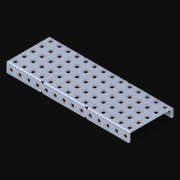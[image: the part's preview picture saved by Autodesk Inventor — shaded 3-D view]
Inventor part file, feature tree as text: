
AUTODESK INVENTOR PART (.ipt)
format: ipt  version: 2021 (Build 250183000, 183)  size: 1,781,760 bytes
history: native  units: in
note: dims shown in document units (in); Inventor stores cm internally (conversion verified against a paired STEP export)
features: extrude x99, other x99, sketch x4, pattern_linear x3
ambient origin geometry x8: Origin, YZ Plane, XZ Plane, XY Plane, X Axis, Y Axis, Z Axis, Center Point
bodies: Solid1 (feature_tree)
feature tree (205):
  pattern_linear  "Rectangular Pattern1"  Spacing1=0.182in  [1 undecoded]
  pattern_linear  "Rectangular Pattern2"  Spacing1=0.046in  [1 undecoded]
  pattern_linear  "Rectangular Pattern3"  Spacing1=0.5in  [1 undecoded]
  extrude  "Extrusion1"  Depth=0.046in
  sketch  "Sketch1"  dims[d0=0.182in]
  other  "Srf1"
  sketch  "Sketch2"  dims[d1=0.046in d2=0.0in]
  other  "Srf2"
  sketch  "Sketch3"  dims[d3=0.182in]
  other  "Srf3"
  other  "Srf4"
  other  "Srf5"
  other  "Srf6"
  other  "Srf7"
  other  "Srf8"
  other  "Srf9"
  other  "Srf10"
  other  "Srf11"
  other  "Srf12"
  other  "Srf13"
  other  "Srf14"
  other  "Srf15"
  other  "Srf16"
  other  "Srf38"
  other  "Srf39"
  other  "Srf40"
  other  "Srf41"
  other  "Srf42"
  other  "Srf43"
  other  "Srf44"
  other  "Srf45"
  other  "Srf46"
  other  "Srf47"
  other  "Srf48"
  other  "Srf49"
  other  "Srf50"
  other  "Srf72"
  other  "Srf73"
  other  "Srf74"
  other  "Srf75"
  other  "Srf76"
  other  "Srf77"
  other  "Srf78"
  other  "Srf79"
  other  "Srf80"
  other  "Srf81"
  other  "Srf82"
  other  "Srf83"
  other  "Srf84"
  other  "Srf85"
  other  "Srf107"
  other  "Srf108"
  other  "Srf109"
  other  "Srf110"
  other  "Srf111"
  other  "Srf112"
  other  "Srf113"
  other  "Srf114"
  other  "Srf115"
  other  "Srf116"
  other  "Srf117"
  other  "Srf118"
  other  "Srf119"
  other  "Srf120"
  other  "Srf142"
  other  "Srf143"
  other  "Srf144"
  other  "Srf145"
  other  "Srf146"
  other  "Srf147"
  other  "Srf148"
  other  "Srf149"
  other  "Srf150"
  other  "Srf151"
  other  "Srf152"
  other  "Srf153"
  other  "Srf154"
  other  "Srf155"
  other  "Srf177"
  other  "Srf178"
  other  "Srf179"
  other  "Srf180"
  other  "Srf181"
  other  "Srf182"
  other  "Srf183"
  other  "Srf184"
  other  "Srf185"
  other  "Srf186"
  other  "Srf187"
  other  "Srf188"
  other  "Srf189"
  other  "Srf190"
  other  "Srf212"
  other  "Srf213"
  other  "Srf214"
  other  "Srf215"
  other  "Srf216"
  other  "Srf217"
  other  "Srf218"
  other  "Srf219"
  other  "Srf220"
  other  "Srf221"
  other  "Srf222"
  other  "Srf223"
  other  "Srf224"
  sketch  "Sketch4"  dims[d4=0.046in d5=0.0in d6=0.182in d7=0.046in d8=0.0in d11=0.5in d12=5.5118in d14=0.5in d15=1.9685in d17=0.5in d18=5.5118in d20=0.5in d21=10.5in d22=0.0in]
  parser-record x1  (decoder bookkeeping rows leaked as tree rows — omitted from the tree; the rows remain in map.json)
  extrude  "ExtrusionSrf1"  Depth=0.046in
  extrude  "ExtrusionSrf2"  Depth=0.046in
  extrude  "ExtrusionSrf3"  Depth=0.046in
  extrude  "ExtrusionSrf4"  Depth=0.046in
  extrude  "ExtrusionSrf5"  Depth=0.046in
  extrude  "ExtrusionSrf6"  TaperAngle=0.0deg  [1 undecoded]
  extrude  "ExtrusionSrf7"  [1 undecoded]
  extrude  "ExtrusionSrf8"  [1 undecoded]
  extrude  "ExtrusionSrf9"  [1 undecoded]
  extrude  "ExtrusionSrf10"  [1 undecoded]
  extrude  "ExtrusionSrf11"  [1 undecoded]
  extrude  "ExtrusionSrf12"  [1 undecoded]
  extrude  "ExtrusionSrf13"  [1 undecoded]
  extrude  "ExtrusionSrf14"  [1 undecoded]
  extrude  "ExtrusionSrf15"  [1 undecoded]
  extrude  "ExtrusionSrf16"  [1 undecoded]
  extrude  "ExtrusionSrf38"  [1 undecoded]
  extrude  "ExtrusionSrf39"  [1 undecoded]
  extrude  "ExtrusionSrf40"  [1 undecoded]
  extrude  "ExtrusionSrf41"  [1 undecoded]
  extrude  "ExtrusionSrf42"  [1 undecoded]
  extrude  "ExtrusionSrf43"  [1 undecoded]
  extrude  "ExtrusionSrf44"  [1 undecoded]
  extrude  "ExtrusionSrf45"  [1 undecoded]
  extrude  "ExtrusionSrf46"  [1 undecoded]
  extrude  "ExtrusionSrf47"  [1 undecoded]
  extrude  "ExtrusionSrf48"  [1 undecoded]
  extrude  "ExtrusionSrf49"  [1 undecoded]
  extrude  "ExtrusionSrf50"  [1 undecoded]
  extrude  "ExtrusionSrf72"  [1 undecoded]
  extrude  "ExtrusionSrf73"  [1 undecoded]
  extrude  "ExtrusionSrf74"  [1 undecoded]
  extrude  "ExtrusionSrf75"  [1 undecoded]
  extrude  "ExtrusionSrf76"  [1 undecoded]
  extrude  "ExtrusionSrf77"  [1 undecoded]
  extrude  "ExtrusionSrf78"  [1 undecoded]
  extrude  "ExtrusionSrf79"  [1 undecoded]
  extrude  "ExtrusionSrf80"  [1 undecoded]
  extrude  "ExtrusionSrf81"  [1 undecoded]
  extrude  "ExtrusionSrf82"  [1 undecoded]
  extrude  "ExtrusionSrf83"  [1 undecoded]
  extrude  "ExtrusionSrf84"  [1 undecoded]
  extrude  "ExtrusionSrf85"  [1 undecoded]
  extrude  "ExtrusionSrf107"  [1 undecoded]
  extrude  "ExtrusionSrf108"  [1 undecoded]
  extrude  "ExtrusionSrf109"  [1 undecoded]
  extrude  "ExtrusionSrf110"  [1 undecoded]
  extrude  "ExtrusionSrf111"  [1 undecoded]
  extrude  "ExtrusionSrf112"  [1 undecoded]
  extrude  "ExtrusionSrf113"  [1 undecoded]
  extrude  "ExtrusionSrf114"  [1 undecoded]
  extrude  "ExtrusionSrf115"  [1 undecoded]
  extrude  "ExtrusionSrf116"  [1 undecoded]
  extrude  "ExtrusionSrf117"  [1 undecoded]
  extrude  "ExtrusionSrf118"  [1 undecoded]
  extrude  "ExtrusionSrf119"  [1 undecoded]
  extrude  "ExtrusionSrf120"  [1 undecoded]
  extrude  "ExtrusionSrf142"  [1 undecoded]
  extrude  "ExtrusionSrf143"  [1 undecoded]
  extrude  "ExtrusionSrf144"  [1 undecoded]
  extrude  "ExtrusionSrf145"  [1 undecoded]
  extrude  "ExtrusionSrf146"  [1 undecoded]
  extrude  "ExtrusionSrf147"  [1 undecoded]
  extrude  "ExtrusionSrf148"  [1 undecoded]
  extrude  "ExtrusionSrf149"  [1 undecoded]
  extrude  "ExtrusionSrf150"  [1 undecoded]
  extrude  "ExtrusionSrf151"  [1 undecoded]
  extrude  "ExtrusionSrf152"  [1 undecoded]
  extrude  "ExtrusionSrf153"  [1 undecoded]
  extrude  "ExtrusionSrf154"  [1 undecoded]
  extrude  "ExtrusionSrf155"  [1 undecoded]
  extrude  "ExtrusionSrf177"  [1 undecoded]
  extrude  "ExtrusionSrf178"  [1 undecoded]
  extrude  "ExtrusionSrf179"  [1 undecoded]
  extrude  "ExtrusionSrf180"  [1 undecoded]
  extrude  "ExtrusionSrf181"  [1 undecoded]
  extrude  "ExtrusionSrf182"  [1 undecoded]
  extrude  "ExtrusionSrf183"  [1 undecoded]
  extrude  "ExtrusionSrf184"  [1 undecoded]
  extrude  "ExtrusionSrf185"  [1 undecoded]
  extrude  "ExtrusionSrf186"  [1 undecoded]
  extrude  "ExtrusionSrf187"  [1 undecoded]
  extrude  "ExtrusionSrf188"  [1 undecoded]
  extrude  "ExtrusionSrf189"  [1 undecoded]
  extrude  "ExtrusionSrf190"  [1 undecoded]
  extrude  "ExtrusionSrf212"  [1 undecoded]
  extrude  "ExtrusionSrf213"  [1 undecoded]
  extrude  "ExtrusionSrf214"  [1 undecoded]
  extrude  "ExtrusionSrf215"  [1 undecoded]
  extrude  "ExtrusionSrf216"  [1 undecoded]
  extrude  "ExtrusionSrf217"  [1 undecoded]
  extrude  "ExtrusionSrf218"  [1 undecoded]
  extrude  "ExtrusionSrf219"  [1 undecoded]
  extrude  "ExtrusionSrf220"  [1 undecoded]
  extrude  "ExtrusionSrf221"  [1 undecoded]
  extrude  "ExtrusionSrf222"  [1 undecoded]
  extrude  "ExtrusionSrf223"  [1 undecoded]
  extrude  "ExtrusionSrf224"  [1 undecoded]
note: 96 required parameter values undecoded (feature->parameter linkage not recoverable at this tier; creation-order binding heuristic only, values carry confidence <= 0.55)
